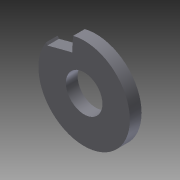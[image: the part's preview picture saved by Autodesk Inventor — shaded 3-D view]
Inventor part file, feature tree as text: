
AUTODESK INVENTOR PART (.ipt)
format: ipt  version: 2014 SP1 (Build 180222100, 222)  size: 91,136 bytes
history: native  units: in
note: dims shown in document units (in); Inventor stores cm internally (conversion verified against a paired STEP export)
features: reference x3, extrude x2, sketch x2
ambient origin geometry x8: Origin, YZ Plane, XZ Plane, XY Plane, X Axis, Y Axis, Z Axis, Center Point
bodies: Solid1 (feature_tree)
feature tree (7):
  extrude  "Extrusion1"  Depth=0.25in
  extrude  "Extrusion2"  Depth=0.3125in
  sketch  "Sketch1"  dims[d0=0.625in d1=0.25in]
  sketch  "Sketch2"  dims[d2=0.08in d3=0.0in d4=0.3125in d5=1.0in d6=0.0in]
  reference  "Reference1"
  reference  "Reference2"
  reference  "Reference3"
